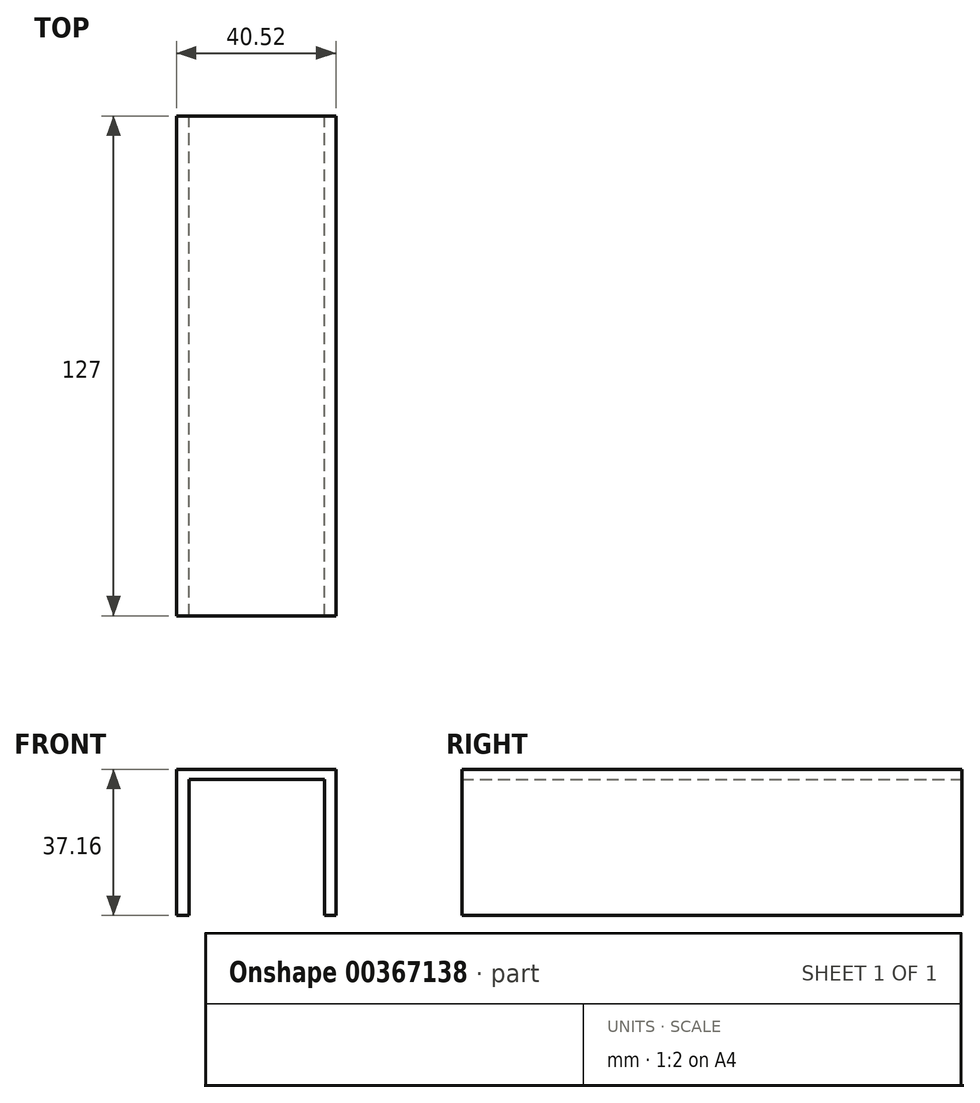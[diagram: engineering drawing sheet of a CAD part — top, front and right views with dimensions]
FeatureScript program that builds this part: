
annotation { "Feature Type Name" : "Feature", "Feature Type Description" : "" }
export const myFeature = defineFeature(function(context is Context, id is Id, definition is map)
    precondition{}
    {
        {
            var Q0;
            Q0=qCreatedBy(makeId("Front.planeOp"),FACE);
            var sketch = newSketch(context, id + "F0", { "sketchPlane" : qUnion([Q0])});
            skLineSegment(sketch, "E0", {"start": v(0, 0) * mm, "end": v(0, 37.16) * mm});
            skLineSegment(sketch, "E1", {"start": v(0, 37.16) * mm, "end": v(40.52, 37.16) * mm});
            skLineSegment(sketch, "E2", {"start": v(40.52, 37.16) * mm, "end": v(40.52, 0) * mm});
            skLineSegment(sketch, "E3", {"start": v(40.52, 0) * mm, "end": v(37.6, 0) * mm});
            skLineSegment(sketch, "E4", {"start": v(37.6, 0) * mm, "end": v(37.6, 34.54) * mm});
            skLineSegment(sketch, "E5", {"start": v(37.6, 34.54) * mm, "end": v(3.2, 34.54) * mm});
            skLineSegment(sketch, "E6", {"start": v(3.2, 34.54) * mm, "end": v(3.2, 0) * mm});
            skLineSegment(sketch, "E7", {"start": v(3.2, 0) * mm, "end": v(0, 0) * mm});
            skLineSegment(sketch, "E8", {"start": v(37.6, 0) * mm, "end": v(40.52, 0) * mm});
            skSolve(sketch);
        }
        {
            var Q0;
            Q0 = qSketchRegion(id + "F0", true);
            extrude(context, id + "F1", {"entities" : qUnion([Q0]), "depth" : 127 * mm});
        }
    });
